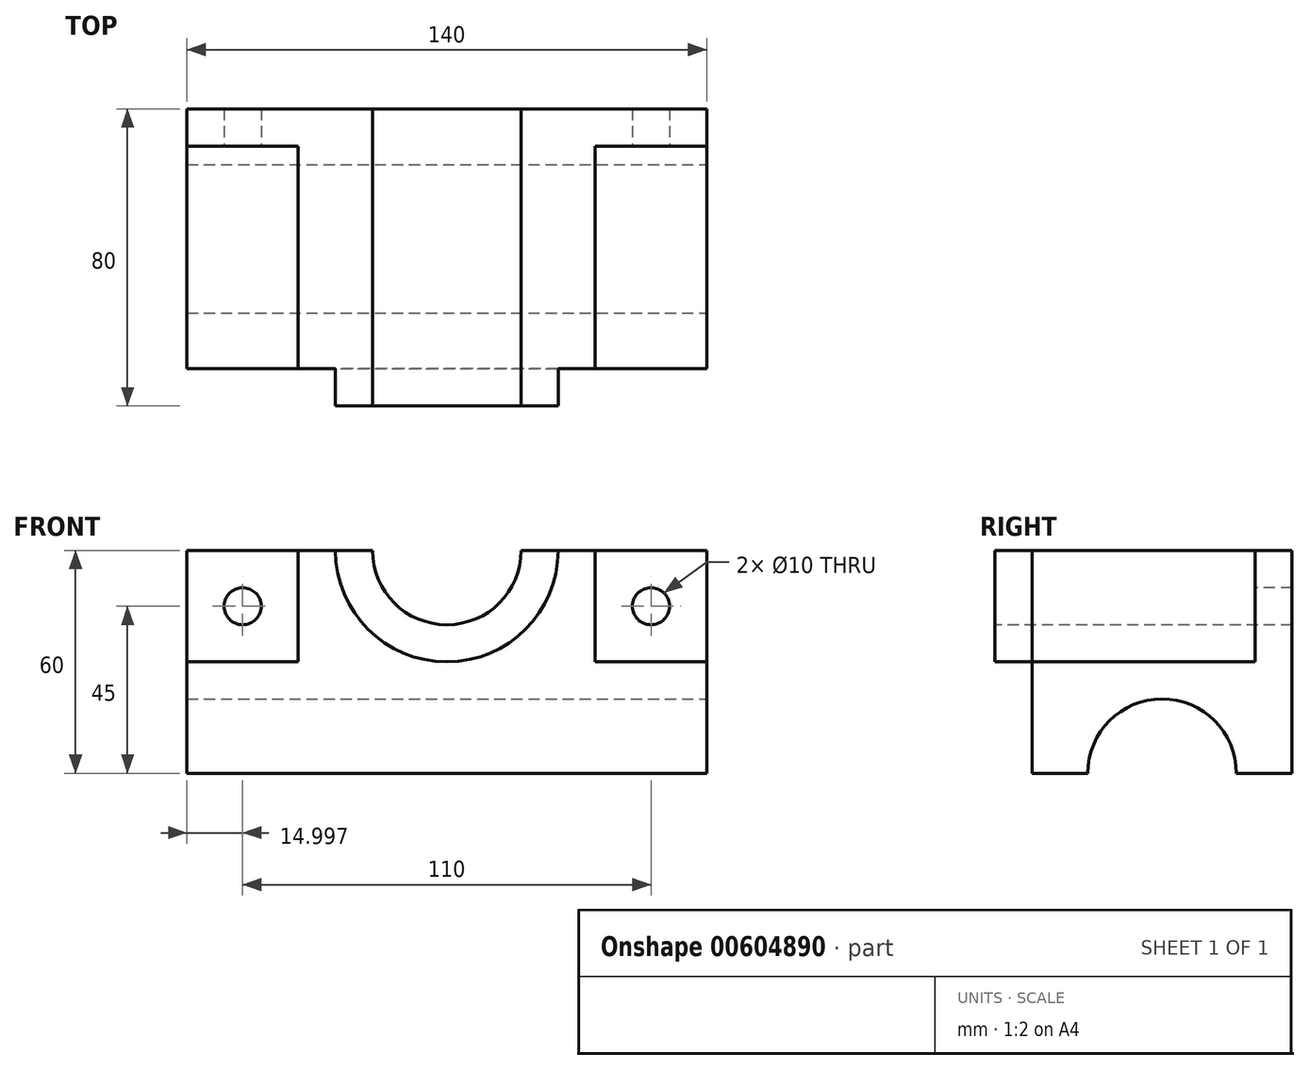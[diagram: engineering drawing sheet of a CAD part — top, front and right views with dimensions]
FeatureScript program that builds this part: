
annotation { "Feature Type Name" : "Feature", "Feature Type Description" : "" }
export const myFeature = defineFeature(function(context is Context, id is Id, definition is map)
    precondition{}
    {
        {
            var Q0;
            Q0=qCreatedBy(makeId("Top.planeOp"),FACE);
            var sketch = newSketch(context, id + "F0", { "sketchPlane" : qUnion([Q0])});
            skLineSegment(sketch, "E0.bottom", {"start": v(-76.8, 44.7) * mm, "end": v(63.2, 44.7) * mm});
            skLineSegment(sketch, "E0.top", {"start": v(-76.8, -25.3) * mm, "end": v(63.2, -25.3) * mm});
            skLineSegment(sketch, "E0.left", {"start": v(-76.8, 44.7) * mm, "end": v(-76.8, -25.3) * mm});
            skLineSegment(sketch, "E0.right", {"start": v(63.2, 44.7) * mm, "end": v(63.2, -25.3) * mm});
            skSolve(sketch);
        }
        {
            var Q0;
            Q0=makeQuery(id+"F0.imprint","IMPRINT",FACE,{"disambiguationData":[TD([[makeQuery(id+"F0.imprint","IMPRINT",EDGE,{"derivedFrom":sQuery(id+"F0.wireOp",EDGE,"E0.bottom")}),-1.0]])]});
            extrude(context, id + "F1", {"entities" : qUnion([Q0]), "depth" : 60 * mm, "offsetDistance" : 25 * mm});
        }
        {
            var Q0;
            Q0=makeQuery(id+"F1.opExtrude","SWEPT_FACE",FACE,{"disambiguationData":[OSD([sQuery(id+"F0.wireOp",EDGE,"E0.right")])]});
            var sketch = newSketch(context, id + "F2", { "sketchPlane" : qUnion([Q0])});
            skCircle(sketch, "E1", {"center": v(9.7, 0) * mm, "radius": 20 * mm});
            skSolve(sketch);
        }
        {
            var Q0;
            Q0 = qSketchRegion(id + "F2", true);
            extrude(context, id + "F3", {"entities" : qUnion([Q0]), "operationType" : NewBodyOperationType.REMOVE, "oppositeDirection" : true, "depth" : 144.4 * mm, "offsetDistance" : 25 * mm});
        }
        {
            var Q0;
            Q0=makeQuery(id+"F1.opExtrude","CAP_FACE",FACE,{"disambiguationData":[OSD([sQuery(id+"F0.wireOp",EDGE,"E0.bottom"),sQuery(id+"F0.wireOp",EDGE,"E0.top"),sQuery(id+"F0.wireOp",EDGE,"E0.left"),sQuery(id+"F0.wireOp",EDGE,"E0.right")])],"isStart":false});
            var sketch = newSketch(context, id + "F4", { "sketchPlane" : qUnion([Q0])});
            skLineSegment(sketch, "E2.bottom", {"start": v(63.2, -25.3) * mm, "end": v(33.2, -25.3) * mm});
            skLineSegment(sketch, "E2.top", {"start": v(63.2, 34.7) * mm, "end": v(33.2, 34.7) * mm});
            skLineSegment(sketch, "E2.left", {"start": v(63.2, -25.3) * mm, "end": v(63.2, 34.7) * mm});
            skLineSegment(sketch, "E2.right", {"start": v(33.2, -25.3) * mm, "end": v(33.2, 34.7) * mm});
            skSolve(sketch);
        }
        {
            var Q0;
            Q0 = qSketchRegion(id + "F4", true);
            extrude(context, id + "F5", {"entities" : qUnion([Q0]), "operationType" : NewBodyOperationType.REMOVE, "oppositeDirection" : true, "depth" : 30 * mm, "offsetDistance" : 25 * mm});
        }
        {
            var Q0;
            Q0=makeQuery(id+"F5.boolean.opBoolean","COPY",FACE,{"derivedFrom":makeQuery(id+"F5.opExtrude","SWEPT_FACE",FACE,{"disambiguationData":[OSD([sQuery(id+"F4.wireOp",EDGE,"E2.top")])]})});
            var sketch = newSketch(context, id + "F6", { "sketchPlane" : qUnion([Q0])});
            skLineSegment(sketch, "E3", {"start": v(48.2, 30) * mm, "end": v(48.2, 45) * mm});
            skCircle(sketch, "E4", {"center": v(48.2, 45) * mm, "radius": 5 * mm});
            skSolve(sketch);
        }
        {
            var Q0;
            Q0=makeQuery(id+"F6.imprint","IMPRINT",FACE,{"disambiguationData":[TD([[makeQuery(id+"F6.imprint","IMPRINT",EDGE,{"derivedFrom":sQuery(id+"F6.wireOp",EDGE,"E4")}),1.0]])]});
            var Q1;
            Q1=sQuery(id+"F6.wireOp",EDGE,"E4");
            extrude(context, id + "F7", {"entities" : qUnion([Q0]), "operationType" : NewBodyOperationType.REMOVE, "surfaceEntities" : qUnion([Q1]), "oppositeDirection" : true, "depth" : 25 * mm, "offsetDistance" : 25 * mm});
        }
        {
            var Q0;
            Q0=makeQuery(id+"F1.opExtrude","SWEPT_FACE",FACE,{"disambiguationData":[OSD([sQuery(id+"F0.wireOp",EDGE,"E0.bottom")])]});
            var sketch = newSketch(context, id + "F8", { "sketchPlane" : qUnion([Q0])});
            skCircle(sketch, "E5", {"center": v(6.8, 60) * mm, "radius": 30 * mm});
            skSolve(sketch);
        }
        {
            var Q0;
            Q0 = qSketchRegion(id + "F8", true);
            extrude(context, id + "F9", {"entities" : qUnion([Q0]), "operationType" : NewBodyOperationType.ADD, "oppositeDirection" : true, "depth" : 80 * mm, "offsetDistance" : 25 * mm});
        }
        {
            var Q0;
            Q0=makeQuery(id+"F9.opExtrude","CAP_FACE",FACE,{"disambiguationData":[OSD([sQuery(id+"F8.wireOp",EDGE,"E5")])],"isStart":false});
            var sketch = newSketch(context, id + "F10", { "sketchPlane" : qUnion([Q0])});
            skCircle(sketch, "E6", {"center": v(-6.8, 60) * mm, "radius": 20 * mm});
            skSolve(sketch);
        }
        {
            var Q0;
            Q0 = qSketchRegion(id + "F10", true);
            extrude(context, id + "F11", {"entities" : qUnion([Q0]), "operationType" : NewBodyOperationType.REMOVE, "oppositeDirection" : true, "depth" : 80 * mm, "offsetDistance" : 25 * mm});
        }
        {
            var Q0;
            Q0=makeQuery(id+"F9.opExtrude","CAP_FACE",FACE,{"disambiguationData":[OSD([sQuery(id+"F8.wireOp",EDGE,"E5")])],"isStart":false});
            var sketch = newSketch(context, id + "F12", { "sketchPlane" : qUnion([Q0])});
            skLineSegment(sketch, "E7.bottom", {"start": v(-6.8, 60) * mm, "end": v(33.06, 60) * mm});
            skLineSegment(sketch, "E7.top", {"start": v(-6.8, 91.38) * mm, "end": v(33.06, 91.38) * mm});
            skLineSegment(sketch, "E7.left", {"start": v(-6.8, 60) * mm, "end": v(-6.8, 91.38) * mm});
            skLineSegment(sketch, "E7.right", {"start": v(33.06, 60) * mm, "end": v(33.06, 91.38) * mm});
            skSolve(sketch);
        }
        {
            var Q0;
            Q0 = qSketchRegion(id + "F12", true);
            extrude(context, id + "F13", {"entities" : qUnion([Q0]), "operationType" : NewBodyOperationType.REMOVE, "oppositeDirection" : true, "depth" : 80 * mm, "offsetDistance" : 25 * mm});
        }
        {
            var Q0;
            Q0=makeQuery(id+"F9.opExtrude","CAP_FACE",FACE,{"disambiguationData":[OSD([sQuery(id+"F8.wireOp",EDGE,"E5")])],"isStart":false});
            var sketch = newSketch(context, id + "F14", { "sketchPlane" : qUnion([Q0])});
            skLineSegment(sketch, "E8.bottom", {"start": v(-6.8, 60) * mm, "end": v(-55.42, 60) * mm});
            skLineSegment(sketch, "E8.top", {"start": v(-6.8, 92) * mm, "end": v(-55.42, 92) * mm});
            skLineSegment(sketch, "E8.left", {"start": v(-6.8, 60) * mm, "end": v(-6.8, 92) * mm});
            skLineSegment(sketch, "E8.right", {"start": v(-55.42, 60) * mm, "end": v(-55.42, 92) * mm});
            skSolve(sketch);
        }
        {
            var Q0;
            Q0 = qSketchRegion(id + "F14", true);
            extrude(context, id + "F15", {"entities" : qUnion([Q0]), "operationType" : NewBodyOperationType.REMOVE, "oppositeDirection" : true, "depth" : 80 * mm, "offsetDistance" : 25 * mm});
        }
        {
            var Q0;
            {var subQ0=sQuery(id+"F0.wireOp",EDGE,"E0.left");var subQ1=sQuery(id+"F0.wireOp",EDGE,"E0.top");var subQ3=sQuery(id+"F0.wireOp",EDGE,"E0.bottom");Q0=makeQuery(id+"F15.boolean.opBoolean","MERGE",FACE,{"derivedFrom":[makeQuery(id+"F9.boolean.opBoolean","SPLIT",FACE,{"disambiguationData":[TD([makeQuery(id+"F1.opExtrude","SWEPT_FACE",FACE,{"disambiguationData":[OSD([subQ0])]})])],"derivedFrom":makeQuery(id+"F1.opExtrude","CAP_FACE",FACE,{"disambiguationData":[OSD([subQ3,subQ1,subQ0,sQuery(id+"F0.wireOp",EDGE,"E0.right")])],"isStart":false})}),makeQuery(id+"F15.opExtrude","SWEPT_FACE",FACE,{"disambiguationData":[OSD([sQuery(id+"F14.wireOp",EDGE,"E8.bottom")])]})]});}
            var sketch = newSketch(context, id + "F16", { "sketchPlane" : qUnion([Q0])});
            skLineSegment(sketch, "E9", {"start": v(-76.8, 44.7) * mm, "end": v(-76.8, 34.7) * mm});
            skLineSegment(sketch, "E10.bottom", {"start": v(-76.8, 34.7) * mm, "end": v(-46.8, 34.7) * mm});
            skLineSegment(sketch, "E10.top", {"start": v(-76.8, -25.3) * mm, "end": v(-46.8, -25.3) * mm});
            skLineSegment(sketch, "E10.left", {"start": v(-76.8, 34.7) * mm, "end": v(-76.8, -25.3) * mm});
            skLineSegment(sketch, "E10.right", {"start": v(-46.8, 34.7) * mm, "end": v(-46.8, -25.3) * mm});
            skSolve(sketch);
        }
        {
            var Q0;
            Q0 = qSketchRegion(id + "F16", true);
            extrude(context, id + "F17", {"entities" : qUnion([Q0]), "operationType" : NewBodyOperationType.REMOVE, "oppositeDirection" : true, "depth" : 30 * mm, "offsetDistance" : 25 * mm});
        }
        {
            var Q0;
            Q0=makeQuery(id+"F17.boolean.opBoolean","COPY",FACE,{"derivedFrom":makeQuery(id+"F17.opExtrude","SWEPT_FACE",FACE,{"disambiguationData":[OSD([sQuery(id+"F16.wireOp",EDGE,"E10.bottom")])]})});
            var sketch = newSketch(context, id + "F18", { "sketchPlane" : qUnion([Q0])});
            skLineSegment(sketch, "E11", {"start": v(-61.8, 60) * mm, "end": v(-61.8, 45) * mm});
            skPoint(sketch, "E11.endSnap0", {"position": v(-61.8, 60) * mm});
            skCircle(sketch, "E12", {"center": v(-61.8, 45) * mm, "radius": 5 * mm});
            skSolve(sketch);
        }
        {
            var Q0;
            Q0 = qSketchRegion(id + "F18", true);
            extrude(context, id + "F19", {"entities" : qUnion([Q0]), "operationType" : NewBodyOperationType.REMOVE, "oppositeDirection" : true, "depth" : 10 * mm, "offsetDistance" : 25 * mm});
        }
    });
